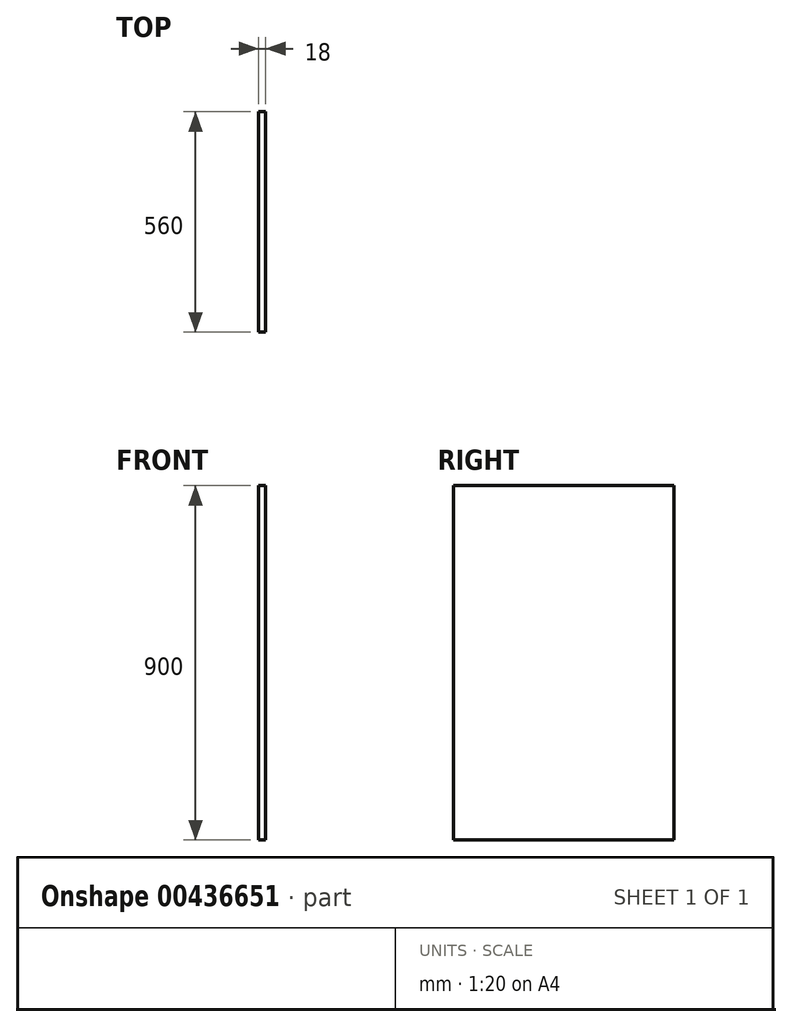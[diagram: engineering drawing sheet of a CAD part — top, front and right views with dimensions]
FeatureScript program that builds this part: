
annotation { "Feature Type Name" : "Feature", "Feature Type Description" : "" }
export const myFeature = defineFeature(function(context is Context, id is Id, definition is map)
    precondition{}
    {
        {
            var Q0;
            Q0=qCreatedBy(makeId("Right.planeOp"),FACE);
            var sketch = newSketch(context, id + "F0", { "sketchPlane" : qUnion([Q0])});
            skLineSegment(sketch, "E0.bottom", {"start": v(280, 450) * mm, "end": v(-280, 450) * mm});
            skLineSegment(sketch, "E0.top", {"start": v(280, -450) * mm, "end": v(-280, -450) * mm});
            skLineSegment(sketch, "E0.left", {"start": v(280, 450) * mm, "end": v(280, -450) * mm});
            skLineSegment(sketch, "E0.right", {"start": v(-280, 450) * mm, "end": v(-280, -450) * mm});
            skPoint(sketch, "E0.middle", {"position": v(0, 0) * mm});
            skSolve(sketch);
        }
        {
            var Q0;
            Q0 = qSketchRegion(id + "F0", true);
            extrude(context, id + "F1", {"entities" : qUnion([Q0]), "depth" : 18 * mm});
        }
    });
